# Revit family: FU_Chair_Sandler_Woodlook 1-9
name_source: partatom
category: Furniture
units: mm (PartAtom-declared; Revit-internal decimal feet)

## family parameters
Always vertical = Yes
Cut with Voids When Loaded = No
OmniClass Number = 23.40.20.00
OmniClass Title = General Furniture and Specialties
Room Calculation Point = No
Shared = No
Work Plane-Based = No

## types (4) — shared parameters
Depth = 585 mm  [stored 1.91929 ft]
Height = 833 mm  [stored 2.73294 ft]
Manufacturer = Sandler
URL = https://www.sandlerseating.com
Width = 510 mm  [stored 1.67323 ft]
zero-valued in all types: Default Elevation

## per-type parameters (varying)
| type | Description | Grab Handle | Model | Stretchers | Upholstery | Woodlook |
| Woodlook 1.9 | Woodlook side chair with frame manufactured entirely from aluminum but with realistic appearance of wood. With stretchers. Highly durable and scratch resistant. Stacks 5 | No | Woodlook 1.9 | Yes | Fabric - Mainline Flax - Upminster MLF20 | Woodlook - 24A Walnut |
| Woodlook 1.9GH | Woodlook side chair with frame manufactured entirely from aluminum but with realistic appearance of wood. With stretchers and back grip handle. Highly durable and scratch resistant. Stacks 5. | Yes | Woodlook 1.9GH | Yes | Fabric - Gravity - Frozen CPC27 | Woodlook - 21A Teak |
| Woodlook 1.9GHWOS | Woodlook side chair with grip handle on back. Frame manufactured entirely from aluminum but with realistic appearance of wood. Highly durable and scratch resistant. Stacks 5. Without stretchers. | Yes | WOODLOOK 1.9GHWOS | No | Fabric - Gravity - Frost CPC32 | Woodlook - 20A Natural Beech |
| Woodlook 1.9WOS | Woodlook side chair with frame manufactured entirely from aluminum but with realistic appearance of wood. Highly durable and scratch resistant. Stacks 6. Without stretchers. | No | Woodlook 1.9WOS | No | Fabric - X2 - Percentage AK016 | Woodlook - 23 Light Walnut |

note: [stored X ft] marks values corroborated as IEEE doubles in the binary element streams (Revit-internal decimal feet)

## geometry (parser evidence)
native form markers: Sweep x3
no freeform markers — native parametric forms only
